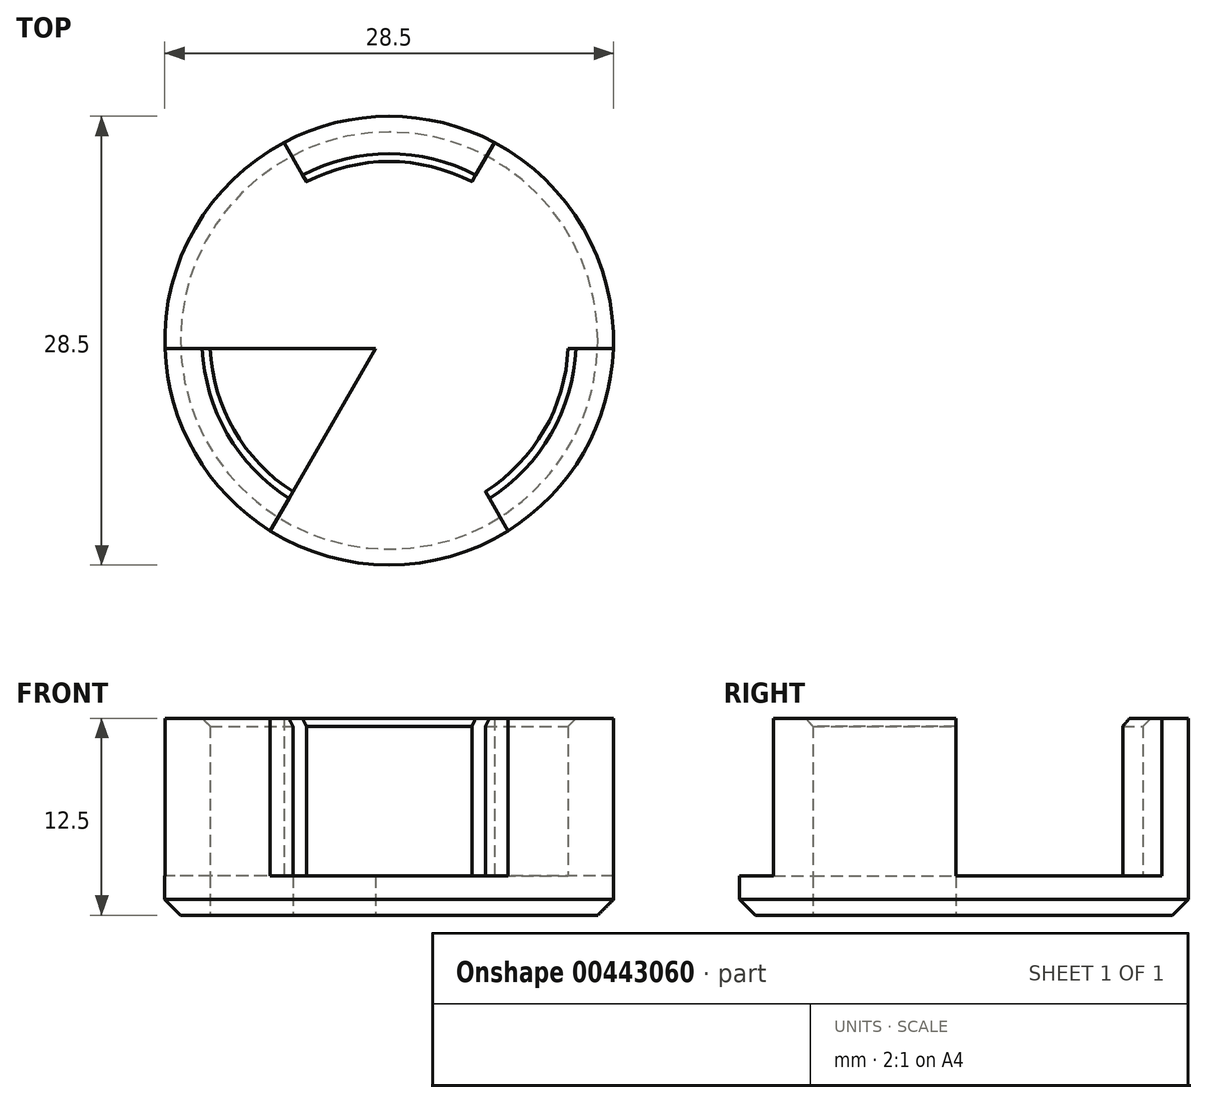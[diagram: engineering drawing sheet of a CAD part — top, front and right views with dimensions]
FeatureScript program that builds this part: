
annotation { "Feature Type Name" : "Feature", "Feature Type Description" : "" }
export const myFeature = defineFeature(function(context is Context, id is Id, definition is map)
    precondition{}
    {
        {
            assignVariable(context, id + "F0", {"name" : "varFase", "anyValue" : 0.5});
        }
        {
            var Q0;
            Q0=qCreatedBy(makeId("Top.planeOp"),FACE);
            var sketch = newSketch(context, id + "F1", { "sketchPlane" : qUnion([Q0])});
            skCircle(sketch, "E0", {"center": v(0, 0) * mm, "radius": 14.25 * mm});
            skCircle(sketch, "E1", {"center": v(0, 0) * mm, "radius": 11.38 * mm});
            skLineSegment(sketch, "E2.bottom", {"start": v(17.5, 0.5) * mm, "end": v(-17.5, 0.5) * mm});
            skLineSegment(sketch, "E2.top", {"start": v(17.5, -0.5) * mm, "end": v(-17.5, -0.5) * mm});
            skLineSegment(sketch, "E2.left", {"start": v(17.5, 0.5) * mm, "end": v(17.5, -0.5) * mm});
            skLineSegment(sketch, "E2.right", {"start": v(-17.5, 0.5) * mm, "end": v(-17.5, -0.5) * mm});
            skLineSegment(sketch, "E3.1.0", {"start": v(-9.18, 14.9) * mm, "end": v(8.32, -15.4) * mm});
            skLineSegment(sketch, "E3.1.1", {"start": v(8.32, -15.4) * mm, "end": v(9.18, -14.9) * mm});
            skLineSegment(sketch, "E3.1.2", {"start": v(-8.32, 15.4) * mm, "end": v(9.18, -14.9) * mm});
            skLineSegment(sketch, "E3.1.3", {"start": v(-9.18, 14.9) * mm, "end": v(-8.32, 15.4) * mm});
            skLineSegment(sketch, "E3.2.0", {"start": v(-8.32, -15.4) * mm, "end": v(9.18, 14.9) * mm});
            skLineSegment(sketch, "E3.2.1", {"start": v(9.18, 14.9) * mm, "end": v(8.32, 15.4) * mm});
            skLineSegment(sketch, "E3.2.2", {"start": v(-9.18, -14.9) * mm, "end": v(8.32, 15.4) * mm});
            skLineSegment(sketch, "E3.2.3", {"start": v(-8.32, -15.4) * mm, "end": v(-9.18, -14.9) * mm});
            skSolve(sketch);
        }
        {
            var Q0;
            {var subQ0=sQuery(id+"F1.wireOp",EDGE,"E3.2.2");var subQ1=sQuery(id+"F1.wireOp",EDGE,"E0");var subQ2=makeQuery(id+"F1.imprint","INTERSECT",VERTEX,{"disambiguationData":[OD(0.0)],"derivedFrom":[subQ1,subQ0]});Q0=makeQuery(id+"F1.imprint","IMPRINT",FACE,{"disambiguationData":[TD([[makeQuery(id+"F1.imprint","IMPRINT",EDGE,{"disambiguationData":[TD([[subQ2,-1.0]])],"derivedFrom":subQ1}),1.0]])]});}
            var Q1;
            {var subQ0=sQuery(id+"F1.wireOp",EDGE,"E3.2.0");var subQ1=sQuery(id+"F1.wireOp",EDGE,"E0");var subQ2=makeQuery(id+"F1.imprint","INTERSECT",VERTEX,{"disambiguationData":[OD(0.0)],"derivedFrom":[subQ1,subQ0]});Q1=makeQuery(id+"F1.imprint","IMPRINT",FACE,{"disambiguationData":[TD([[makeQuery(id+"F1.imprint","IMPRINT",EDGE,{"disambiguationData":[TD([[subQ2,1.0]])],"derivedFrom":subQ1}),1.0]])]});}
            var Q2;
            {var subQ0=sQuery(id+"F1.wireOp",EDGE,"E3.1.2");var subQ1=sQuery(id+"F1.wireOp",EDGE,"E0");var subQ2=makeQuery(id+"F1.imprint","INTERSECT",VERTEX,{"disambiguationData":[OD(1.0)],"derivedFrom":[subQ1,subQ0]});Q2=makeQuery(id+"F1.imprint","IMPRINT",FACE,{"disambiguationData":[TD([[makeQuery(id+"F1.imprint","IMPRINT",EDGE,{"disambiguationData":[TD([[subQ2,-1.0]])],"derivedFrom":subQ1}),1.0]])]});}
            var Q3;
            {var subQ0=sQuery(id+"F1.wireOp",EDGE,"E2.top");var subQ1=sQuery(id+"F1.wireOp",EDGE,"E0");var subQ2=makeQuery(id+"F1.imprint","INTERSECT",VERTEX,{"disambiguationData":[OD(0.0)],"derivedFrom":[subQ1,subQ0]});Q3=makeQuery(id+"F1.imprint","IMPRINT",FACE,{"disambiguationData":[TD([[makeQuery(id+"F1.imprint","IMPRINT",EDGE,{"disambiguationData":[TD([[subQ2,-1.0]])],"derivedFrom":subQ1}),1.0]])]});}
            var Q4;
            {var subQ0=sQuery(id+"F1.wireOp",EDGE,"E3.1.0");var subQ1=sQuery(id+"F1.wireOp",EDGE,"E0");var subQ2=makeQuery(id+"F1.imprint","INTERSECT",VERTEX,{"disambiguationData":[OD(0.0)],"derivedFrom":[subQ1,subQ0]});Q4=makeQuery(id+"F1.imprint","IMPRINT",FACE,{"disambiguationData":[TD([[makeQuery(id+"F1.imprint","IMPRINT",EDGE,{"disambiguationData":[TD([[subQ2,-1.0]])],"derivedFrom":subQ1}),1.0]])]});}
            extrude(context, id + "F2", {"entities" : qUnion([Q0, Q1, Q2, Q3, Q4]), "depth" : 12.5 * mm});
        }
        {
            var Q0;
            Q0=makeQuery(id+"F1.imprint","IMPRINT",FACE,{"disambiguationData":[TD([[makeQuery(id+"F1.imprint","IMPRINT",EDGE,{"derivedFrom":sQuery(id+"F1.wireOp",EDGE,"E0")}),1.0]])]});
            var Q1;
            {var subQ0=sQuery(id+"F1.wireOp",EDGE,"E2.bottom");var subQ1=sQuery(id+"F1.wireOp",EDGE,"E1");var subQ2=makeQuery(id+"F1.imprint","INTERSECT",VERTEX,{"disambiguationData":[OD(0.0)],"derivedFrom":[subQ1,subQ0]});Q1=makeQuery(id+"F1.imprint","IMPRINT",FACE,{"disambiguationData":[TD([[makeQuery(id+"F1.imprint","IMPRINT",EDGE,{"disambiguationData":[TD([[subQ2,-1.0]])],"derivedFrom":subQ1}),1.0]])]});}
            var Q2;
            {var subQ0=sQuery(id+"F1.wireOp",EDGE,"E2.bottom");var subQ1=sQuery(id+"F1.wireOp",EDGE,"E1");var subQ2=makeQuery(id+"F1.imprint","INTERSECT",VERTEX,{"disambiguationData":[OD(0.0)],"derivedFrom":[subQ1,subQ0]});Q2=makeQuery(id+"F1.imprint","IMPRINT",FACE,{"disambiguationData":[TD([[makeQuery(id+"F1.imprint","IMPRINT",EDGE,{"disambiguationData":[TD([[subQ2,1.0]])],"derivedFrom":subQ1}),1.0]])]});}
            var Q3;
            {var subQ0=sQuery(id+"F1.wireOp",EDGE,"E2.top");var subQ1=sQuery(id+"F1.wireOp",EDGE,"E1");var subQ2=makeQuery(id+"F1.imprint","INTERSECT",VERTEX,{"disambiguationData":[OD(0.0)],"derivedFrom":[subQ1,subQ0]});Q3=makeQuery(id+"F1.imprint","IMPRINT",FACE,{"disambiguationData":[TD([[makeQuery(id+"F1.imprint","IMPRINT",EDGE,{"disambiguationData":[TD([[subQ2,-1.0]])],"derivedFrom":subQ1}),1.0]])]});}
            var Q4;
            {var subQ0=sQuery(id+"F1.wireOp",EDGE,"E3.1.0");var subQ1=sQuery(id+"F1.wireOp",EDGE,"E1");var subQ2=makeQuery(id+"F1.imprint","INTERSECT",VERTEX,{"disambiguationData":[OD(0.0)],"derivedFrom":[subQ1,subQ0]});Q4=makeQuery(id+"F1.imprint","IMPRINT",FACE,{"disambiguationData":[TD([[makeQuery(id+"F1.imprint","IMPRINT",EDGE,{"disambiguationData":[TD([[subQ2,-1.0]])],"derivedFrom":subQ1}),1.0]])]});}
            var Q5;
            {var subQ0=sQuery(id+"F1.wireOp",EDGE,"E3.1.2");var subQ1=sQuery(id+"F1.wireOp",EDGE,"E1");var subQ2=makeQuery(id+"F1.imprint","INTERSECT",VERTEX,{"disambiguationData":[OD(0.0)],"derivedFrom":[subQ1,subQ0]});Q5=makeQuery(id+"F1.imprint","IMPRINT",FACE,{"disambiguationData":[TD([[makeQuery(id+"F1.imprint","IMPRINT",EDGE,{"disambiguationData":[TD([[subQ2,-1.0]])],"derivedFrom":subQ1}),1.0]])]});}
            var Q6;
            {var subQ0=sQuery(id+"F1.wireOp",EDGE,"E3.2.2");var subQ1=sQuery(id+"F1.wireOp",EDGE,"E1");var subQ2=makeQuery(id+"F1.imprint","INTERSECT",VERTEX,{"disambiguationData":[OD(0.0)],"derivedFrom":[subQ1,subQ0]});Q6=makeQuery(id+"F1.imprint","IMPRINT",FACE,{"disambiguationData":[TD([[makeQuery(id+"F1.imprint","IMPRINT",EDGE,{"disambiguationData":[TD([[subQ2,-1.0]])],"derivedFrom":subQ1}),1.0]])]});}
            var Q7;
            {var subQ0=sQuery(id+"F1.wireOp",EDGE,"E3.2.0");var subQ1=sQuery(id+"F1.wireOp",EDGE,"E1");var subQ2=makeQuery(id+"F1.imprint","INTERSECT",VERTEX,{"disambiguationData":[OD(0.0)],"derivedFrom":[subQ1,subQ0]});Q7=makeQuery(id+"F1.imprint","IMPRINT",FACE,{"disambiguationData":[TD([[makeQuery(id+"F1.imprint","IMPRINT",EDGE,{"disambiguationData":[TD([[subQ2,-1.0]])],"derivedFrom":subQ1}),1.0]])]});}
            var Q8;
            {var subQ1=sQuery(id+"F1.wireOp",EDGE,"E1");var subQ5=sQuery(id+"F1.wireOp",EDGE,"E3.1.0");var subQ6=makeQuery(id+"F1.imprint","INTERSECT",VERTEX,{"disambiguationData":[OD(1.0)],"derivedFrom":[subQ1,subQ5]});Q8=makeQuery(id+"F1.imprint","IMPRINT",FACE,{"disambiguationData":[TD([[makeQuery(id+"F1.imprint","IMPRINT",EDGE,{"disambiguationData":[TD([[subQ6,-1.0]])],"derivedFrom":subQ1}),1.0]])]});}
            var Q9;
            {var subQ0=sQuery(id+"F1.wireOp",EDGE,"E3.1.2");var subQ1=sQuery(id+"F1.wireOp",EDGE,"E1");var subQ2=makeQuery(id+"F1.imprint","INTERSECT",VERTEX,{"disambiguationData":[OD(1.0)],"derivedFrom":[subQ1,subQ0]});Q9=makeQuery(id+"F1.imprint","IMPRINT",FACE,{"disambiguationData":[TD([[makeQuery(id+"F1.imprint","IMPRINT",EDGE,{"disambiguationData":[TD([[subQ2,-1.0]])],"derivedFrom":subQ1}),1.0]])]});}
            var Q10;
            {var subQ0=sQuery(id+"F1.wireOp",EDGE,"E3.2.0");var subQ1=sQuery(id+"F1.wireOp",EDGE,"E1");var subQ2=makeQuery(id+"F1.imprint","INTERSECT",VERTEX,{"disambiguationData":[OD(1.0)],"derivedFrom":[subQ1,subQ0]});Q10=makeQuery(id+"F1.imprint","IMPRINT",FACE,{"disambiguationData":[TD([[makeQuery(id+"F1.imprint","IMPRINT",EDGE,{"disambiguationData":[TD([[subQ2,-1.0]])],"derivedFrom":subQ1}),1.0]])]});}
            var Q11;
            {var subQ1=sQuery(id+"F1.wireOp",EDGE,"E1");var subQ7=sQuery(id+"F1.wireOp",EDGE,"E3.2.2");var subQ9=makeQuery(id+"F1.imprint","INTERSECT",VERTEX,{"disambiguationData":[OD(1.0)],"derivedFrom":[subQ1,subQ7]});Q11=makeQuery(id+"F1.imprint","IMPRINT",FACE,{"disambiguationData":[TD([[makeQuery(id+"F1.imprint","IMPRINT",EDGE,{"disambiguationData":[TD([[subQ9,-1.0]])],"derivedFrom":subQ1}),1.0]])]});}
            var Q12;
            {var subQ7=sQuery(id+"F1.wireOp",EDGE,"E3.1.2");var subQ8=sQuery(id+"F1.wireOp",EDGE,"E2.bottom");var subQ9=makeQuery(id+"F1.imprint","INTERSECT",VERTEX,{"derivedFrom":[subQ8,subQ7]});Q12=makeQuery(id+"F1.imprint","IMPRINT",FACE,{"disambiguationData":[TD([[makeQuery(id+"F1.imprint","IMPRINT",EDGE,{"disambiguationData":[TD([[subQ9,-1.0]])],"derivedFrom":subQ8}),1.0]])]});}
            var Q13;
            {var subQ1=sQuery(id+"F1.wireOp",EDGE,"E1");var subQ5=sQuery(id+"F1.wireOp",EDGE,"E2.bottom");var subQ6=makeQuery(id+"F1.imprint","INTERSECT",VERTEX,{"disambiguationData":[OD(1.0)],"derivedFrom":[subQ1,subQ5]});Q13=makeQuery(id+"F1.imprint","IMPRINT",FACE,{"disambiguationData":[TD([[makeQuery(id+"F1.imprint","IMPRINT",EDGE,{"disambiguationData":[TD([[subQ6,-1.0]])],"derivedFrom":subQ1}),1.0]])]});}
            var Q14;
            {var subQ0=sQuery(id+"F1.wireOp",EDGE,"E3.2.0");var subQ1=sQuery(id+"F1.wireOp",EDGE,"E2.top");var subQ2=makeQuery(id+"F1.imprint","INTERSECT",VERTEX,{"derivedFrom":[subQ1,subQ0]});Q14=makeQuery(id+"F1.imprint","IMPRINT",FACE,{"disambiguationData":[TD([[makeQuery(id+"F1.imprint","IMPRINT",EDGE,{"disambiguationData":[TD([[subQ2,-1.0]])],"derivedFrom":subQ1}),1.0]])]});}
            var Q15;
            {var subQ0=sQuery(id+"F1.wireOp",EDGE,"E3.1.0");var subQ1=sQuery(id+"F1.wireOp",EDGE,"E2.top");var subQ2=makeQuery(id+"F1.imprint","INTERSECT",VERTEX,{"derivedFrom":[subQ1,subQ0]});Q15=makeQuery(id+"F1.imprint","IMPRINT",FACE,{"disambiguationData":[TD([[makeQuery(id+"F1.imprint","IMPRINT",EDGE,{"disambiguationData":[TD([[subQ2,-1.0]])],"derivedFrom":subQ1}),-1.0]])]});}
            var Q16;
            {var subQ0=sQuery(id+"F1.wireOp",EDGE,"E3.2.2");var subQ1=sQuery(id+"F1.wireOp",EDGE,"E2.bottom");var subQ2=makeQuery(id+"F1.imprint","INTERSECT",VERTEX,{"derivedFrom":[subQ1,subQ0]});Q16=makeQuery(id+"F1.imprint","IMPRINT",FACE,{"disambiguationData":[TD([[makeQuery(id+"F1.imprint","IMPRINT",EDGE,{"disambiguationData":[TD([[subQ2,-1.0]])],"derivedFrom":subQ1}),1.0]])]});}
            var Q17;
            {var subQ0=sQuery(id+"F1.wireOp",EDGE,"E3.1.2");var subQ1=sQuery(id+"F1.wireOp",EDGE,"E2.bottom");var subQ2=makeQuery(id+"F1.imprint","INTERSECT",VERTEX,{"derivedFrom":[subQ1,subQ0]});Q17=makeQuery(id+"F1.imprint","IMPRINT",FACE,{"disambiguationData":[TD([[makeQuery(id+"F1.imprint","IMPRINT",EDGE,{"disambiguationData":[TD([[subQ2,-1.0]])],"derivedFrom":subQ1}),-1.0]])]});}
            var Q18;
            {var subQ0=sQuery(id+"F1.wireOp",EDGE,"E3.2.0");var subQ1=sQuery(id+"F1.wireOp",EDGE,"E2.bottom");var subQ2=makeQuery(id+"F1.imprint","INTERSECT",VERTEX,{"derivedFrom":[subQ1,subQ0]});Q18=makeQuery(id+"F1.imprint","IMPRINT",FACE,{"disambiguationData":[TD([[makeQuery(id+"F1.imprint","IMPRINT",EDGE,{"disambiguationData":[TD([[subQ2,-1.0]])],"derivedFrom":subQ1}),1.0]])]});}
            var Q19;
            {var subQ0=sQuery(id+"F1.wireOp",EDGE,"E3.1.2");var subQ1=sQuery(id+"F1.wireOp",EDGE,"E2.top");var subQ2=makeQuery(id+"F1.imprint","INTERSECT",VERTEX,{"derivedFrom":[subQ1,subQ0]});Q19=makeQuery(id+"F1.imprint","IMPRINT",FACE,{"disambiguationData":[TD([[makeQuery(id+"F1.imprint","IMPRINT",EDGE,{"disambiguationData":[TD([[subQ2,-1.0]])],"derivedFrom":subQ1}),-1.0]])]});}
            extrude(context, id + "F3", {"entities" : qUnion([Q0, Q1, Q2, Q3, Q4, Q5, Q6, Q7, Q8, Q9, Q10, Q11, Q12, Q13, Q14, Q15, Q16, Q17, Q18, Q19]), "operationType" : NewBodyOperationType.ADD, "depth" : 2.5 * mm});
        }
        {
            var Q0;
            Q0=makeQuery(id+"F2.opExtrude","CAP_EDGE",EDGE,{"disambiguationData":[OSD([sQuery(id+"F1.wireOp",EDGE,"E1")])],"isStart":false});
            chamfer(context, id + "F4", {"entities" : qUnion([Q0]), "width" : (getVariable(context, 'varFase')) * mm, "tangentPropagation" : true});
        }
        {
            var Q0;
            {var subQ5=sQuery(id+"F1.wireOp",EDGE,"E2.right");Q0=makeQuery(id+"F1.imprint","IMPRINT",FACE,{"disambiguationData":[TD([[makeQuery(id+"F1.imprint","IMPRINT",EDGE,{"derivedFrom":subQ5}),1.0]])]});}
            var Q1;
            {var subQ0=sQuery(id+"F1.wireOp",EDGE,"E2.bottom");var subQ1=sQuery(id+"F1.wireOp",EDGE,"E0");var subQ2=makeQuery(id+"F1.imprint","INTERSECT",VERTEX,{"disambiguationData":[OD(0.0)],"derivedFrom":[subQ1,subQ0]});Q1=makeQuery(id+"F1.imprint","IMPRINT",FACE,{"disambiguationData":[TD([[makeQuery(id+"F1.imprint","IMPRINT",EDGE,{"disambiguationData":[TD([[subQ2,-1.0]])],"derivedFrom":subQ1}),1.0]])]});}
            var Q2;
            {var subQ0=sQuery(id+"F1.wireOp",EDGE,"E2.bottom");var subQ1=sQuery(id+"F1.wireOp",EDGE,"E1");var subQ2=makeQuery(id+"F1.imprint","INTERSECT",VERTEX,{"disambiguationData":[OD(0.0)],"derivedFrom":[subQ1,subQ0]});Q2=makeQuery(id+"F1.imprint","IMPRINT",FACE,{"disambiguationData":[TD([[makeQuery(id+"F1.imprint","IMPRINT",EDGE,{"disambiguationData":[TD([[subQ2,-1.0]])],"derivedFrom":subQ1}),1.0]])]});}
            var Q3;
            {var subQ0=sQuery(id+"F1.wireOp",EDGE,"E2.bottom");var subQ1=sQuery(id+"F1.wireOp",EDGE,"E0");var subQ2=makeQuery(id+"F1.imprint","INTERSECT",VERTEX,{"disambiguationData":[OD(1.0)],"derivedFrom":[subQ1,subQ0]});Q3=makeQuery(id+"F1.imprint","IMPRINT",FACE,{"disambiguationData":[TD([[makeQuery(id+"F1.imprint","IMPRINT",EDGE,{"disambiguationData":[TD([[subQ2,1.0]])],"derivedFrom":subQ1}),1.0]])]});}
            var Q4;
            {var subQ5=sQuery(id+"F1.wireOp",EDGE,"E2.left");Q4=makeQuery(id+"F1.imprint","IMPRINT",FACE,{"disambiguationData":[TD([[makeQuery(id+"F1.imprint","IMPRINT",EDGE,{"derivedFrom":subQ5}),-1.0]])]});}
            extrude(context, id + "F5", {"entities" : qUnion([Q0, Q1, Q2, Q3, Q4]), "operationType" : NewBodyOperationType.REMOVE, "depth" : 25 * mm, "hasSecondDirection" : true, "secondDirectionOppositeDirection" : true, "secondDirectionDepth" : -2.5 * mm});
        }
        {
            var Q0;
            {var subQ0=sQuery(id+"F1.wireOp",EDGE,"E0");var subQ1=sQuery(id+"F1.wireOp",EDGE,"E3.1.2");var subQ2=sQuery(id+"F1.wireOp",EDGE,"E2.top");var subQ3=sQuery(id+"F1.wireOp",EDGE,"E3.2.2");Q0=makeQuery(id+"F3.boolean.opBoolean","MERGE",EDGE,{"derivedFrom":[makeQuery(id+"F2.opExtrude","CAP_EDGE",EDGE,{"disambiguationData":[OSD([subQ0]),TDD([makeQuery(id+"F1.imprint","IMPRINT",EDGE,{"disambiguationData":[TD([[makeQuery(id+"F1.imprint","INTERSECT",VERTEX,{"disambiguationData":[OD(0.0)],"derivedFrom":[subQ0,sQuery(id+"F1.wireOp",EDGE,"E3.2.0")]}),1.0]])],"derivedFrom":subQ0})])],"isStart":true}),makeQuery(id+"F2.opExtrude","CAP_EDGE",EDGE,{"disambiguationData":[OSD([subQ0]),TDD([makeQuery(id+"F1.imprint","IMPRINT",EDGE,{"disambiguationData":[TD([[makeQuery(id+"F1.imprint","INTERSECT",VERTEX,{"disambiguationData":[OD(0.0)],"derivedFrom":[subQ0,subQ3]}),-1.0]])],"derivedFrom":subQ0})])],"isStart":true}),makeQuery(id+"F2.opExtrude","CAP_EDGE",EDGE,{"disambiguationData":[OSD([subQ0]),TDD([makeQuery(id+"F1.imprint","IMPRINT",EDGE,{"disambiguationData":[TD([[makeQuery(id+"F1.imprint","INTERSECT",VERTEX,{"disambiguationData":[OD(0.0)],"derivedFrom":[subQ0,sQuery(id+"F1.wireOp",EDGE,"E3.1.0")]}),-1.0]])],"derivedFrom":subQ0})])],"isStart":true}),makeQuery(id+"F2.opExtrude","CAP_EDGE",EDGE,{"disambiguationData":[OSD([subQ0]),TDD([makeQuery(id+"F1.imprint","IMPRINT",EDGE,{"disambiguationData":[TD([[makeQuery(id+"F1.imprint","INTERSECT",VERTEX,{"disambiguationData":[OD(0.0)],"derivedFrom":[subQ0,subQ2]}),-1.0]])],"derivedFrom":subQ0})])],"isStart":true}),makeQuery(id+"F2.opExtrude","CAP_EDGE",EDGE,{"disambiguationData":[OSD([subQ0]),TDD([makeQuery(id+"F1.imprint","IMPRINT",EDGE,{"disambiguationData":[TD([[makeQuery(id+"F1.imprint","INTERSECT",VERTEX,{"disambiguationData":[OD(1.0)],"derivedFrom":[subQ0,subQ1]}),-1.0]])],"derivedFrom":subQ0})])],"isStart":true}),makeQuery(id+"F3.opExtrude","CAP_EDGE",EDGE,{"disambiguationData":[OSD([subQ0])],"isStart":true})]});}
            chamfer(context, id + "F6", {"entities" : qUnion([Q0]), "width" : 1 * mm, "tangentPropagation" : true});
        }
    });
